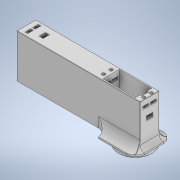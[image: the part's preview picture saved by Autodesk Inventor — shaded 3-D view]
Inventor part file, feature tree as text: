
AUTODESK INVENTOR PART (.ipt)
format: ipt  version: 2022 (Build 260153000, 153)  size: 1,305,600 bytes
history: native  units: mm
features: sketch x39, extrude x38, projected_geometry x14, fillet x13, other x10, pattern_circular x2, mirror x1
ambient origin geometry x8: Origin, YZ Plane, XZ Plane, XY Plane, X Axis, Y Axis, Z Axis, Center Point
bodies: Body1 (feature_tree)
feature tree (117):
  other  "Твердое тело1"
  extrude  "Выдавливание1"  Depth=29.25mm
  extrude  "Выдавливание2"  Depth=59.05mm
  extrude  "Выдавливание3"  Depth=15.0mm
  other  "РабПлоскость1"
  extrude  "Выдавливание4"  Depth=3.0mm
  other  "РабПлоскость2"
  other  "РабПлоскость3"
  other  "РабПлоскость5"
  extrude  "Выдавливание10"  Depth=41.0mm TaperAngle=0.0deg
  extrude  "Выдавливание11"  Depth=3.0mm TaperAngle=0.0deg
  fillet  "Сопряжение8"  Radius=4.2mm
  extrude  "Выдавливание12"  Depth=20.0mm TaperAngle=0.0deg
  fillet  "Сопряжение9"  [1 undecoded]
  mirror  "Зеркальное отражение2"
  extrude  "Выдавливание13"  Depth=7.15mm
  extrude  "Выдавливание15"  Depth=20.0mm
  sketch  "Эскиз18"
  other  "РабОсь1"
  extrude  "Выдавливание16"  Depth=3.25mm TaperAngle=0.0deg
  fillet  "Сопряжение12"  Radius=7.0mm
  pattern_circular  "Круговой массив1"  [2 undecoded]
  fillet  "Сопряжение14"  Radius=4.0mm
  extrude  "Выдавливание24"  Depth=1.95mm
  extrude  "Выдавливание25"  Depth=10.0mm
  extrude  "Выдавливание26"  Depth=2.0mm
  other  "РабПлоскость8"
  extrude  "Выдавливание27"  Depth=1.5mm TaperAngle=0.0deg
  extrude  "Выдавливание28"  Depth=1.0mm
  extrude  "Выдавливание29"  Depth=0.2mm
  extrude  "Выдавливание30"  Depth=19.0mm
  extrude  "Выдавливание31"  Depth=68.0mm
  extrude  "Выдавливание32"  Depth=3.5mm
  sketch  "Эскиз36"
  other  "РабТочка1"
  extrude  "Выдавливание33"  Depth=5.0mm
  extrude  "Выдавливание34"  Depth=4.1mm
  extrude  "Выдавливание35"  Depth=7.95mm
  extrude  "Выдавливание36"  Depth=28.1mm
  extrude  "Выдавливание37"  Depth=4.0mm TaperAngle=0.0deg
  other  "РабПлоскость9"
  extrude  "Выдавливание38"  Depth=18.75mm
  extrude  "Выдавливание39"  Depth=37.8mm
  extrude  "Выдавливание40"  Depth=2.0mm
  extrude  "Выдавливание41"  Depth=6.0mm TaperAngle=0.0deg
  extrude  "Выдавливание42"  Depth=0.5mm
  fillet  "Сопряжение21"  Radius=5.4mm
  fillet  "Сопряжение22"  Radius=0.7mm
  fillet  "Сопряжение23"  Radius=120.0mm
  extrude  "Выдавливание43"  Depth=1.5mm
  fillet  "Сопряжение24"  Radius=47.7mm
  pattern_circular  "Круговой массив2"  [2 undecoded]
  fillet  "Сопряжение25"  Radius=6.0mm
  extrude  "Выдавливание44"  Depth=1.5mm
  fillet  "Сопряжение27"  Radius=4.0mm
  extrude  "Выдавливание17"  Depth=4.0mm
  fillet  "Сопряжение15"  Radius=35.2mm
  extrude  "Выдавливание18"  Depth=9.8mm
  extrude  "Выдавливание19"  Depth=6.15mm
  extrude  "Выдавливание20"  Depth=5.8mm TaperAngle=0.0deg
  extrude  "Выдавливание21"  Depth=13.0mm
  fillet  "Сопряжение16"  Radius=1.9mm
  extrude  "Выдавливание22"  Depth=7.5mm
  other  "РабПлоскость7"
  extrude  "Выдавливание23"  Depth=4.8mm
  fillet  "Сопряжение17"  Radius=3.0mm
  sketch  "Эскиз14"
  sketch  "Эскиз1"
  sketch  "Эскиз2"
  sketch  "Эскиз3"
  sketch  "Эскиз4"
  sketch  "Эскиз10"
  sketch  "Эскиз11"
  sketch  "Эскиз13"
  sketch  "Эскиз15"
  sketch  "Эскиз17"
  sketch  "Эскиз19"
  projected_geometry  "Спроецированная петля1"
  sketch  "Эскиз20"
  projected_geometry  "Спроецированная петля2"
  sketch  "Эскиз21"
  projected_geometry  "Спроецированная петля3"
  sketch  "Эскиз22"
  sketch  "Эскиз23"
  sketch  "Эскиз25"
  projected_geometry  "Спроецированная петля4"
  sketch  "Эскиз26"
  projected_geometry  "Спроецированная петля5"
  sketch  "Эскиз27"
  projected_geometry  "Спроецированная петля6"
  sketch  "Эскиз28"
  projected_geometry  "Спроецированная петля7"
  sketch  "Эскиз29"
  projected_geometry  "Спроецированная петля8"
  sketch  "Эскиз31"
  projected_geometry  "Спроецированная петля9"
  sketch  "Эскиз32"
  sketch  "Эскиз33"
  sketch  "Эскиз34"
  sketch  "Эскиз35"
  sketch  "Эскиз37"
  projected_geometry  "Спроецированная петля10"
  sketch  "Эскиз38"
  sketch  "Эскиз39"
  sketch  "Эскиз40"
  sketch  "Эскиз41"
  sketch  "Эскиз42"
  projected_geometry  "Спроецированная петля11"
  sketch  "Эскиз43"
  sketch  "Эскиз44"
  projected_geometry  "Спроецированная петля12"
  sketch  "Эскиз45"
  projected_geometry  "Спроецированная петля13"
  projected_geometry  "Спроецированная петля14"
  sketch  "Эскиз46"
  sketch  "Эскиз47"
  sketch  "Эскиз48"
note: 5 required parameter values undecoded (feature->parameter linkage not recoverable at this tier; creation-order binding heuristic only, values carry confidence <= 0.55)
